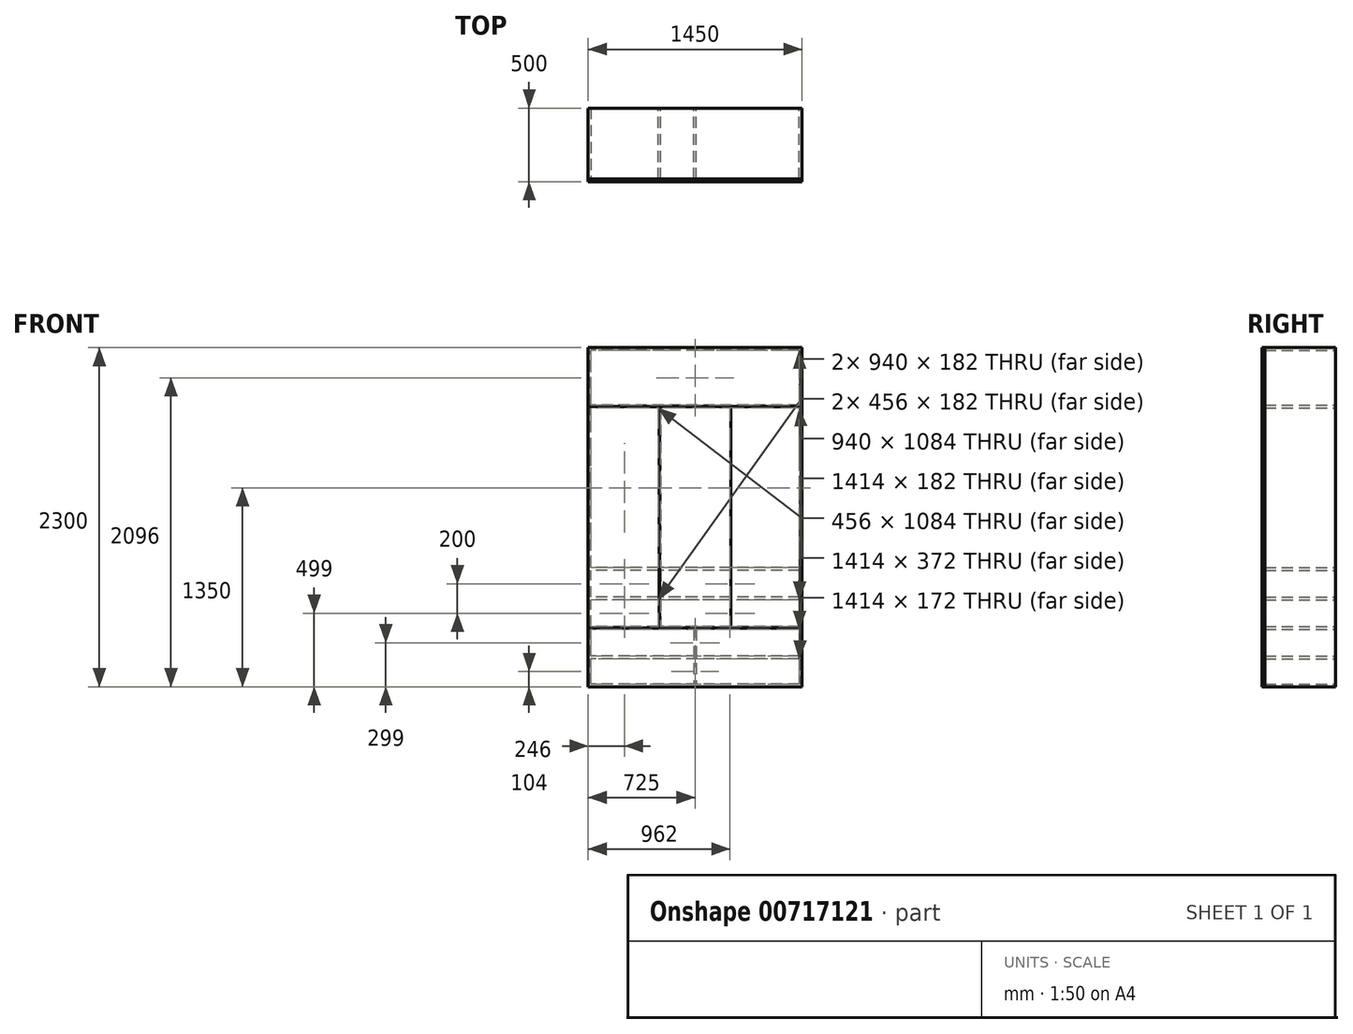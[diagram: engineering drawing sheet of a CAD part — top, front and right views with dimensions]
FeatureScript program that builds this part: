
annotation { "Feature Type Name" : "Feature", "Feature Type Description" : "" }
export const myFeature = defineFeature(function(context is Context, id is Id, definition is map)
    precondition{}
    {
        {
            var Q0;
            Q0=qCreatedBy(makeId("Front.planeOp"),FACE);
            var sketch = newSketch(context, id + "F0", { "sketchPlane" : qUnion([Q0])});
            skLineSegment(sketch, "E0.bottom", {"start": v(725, -1150) * mm, "end": v(-725, -1150) * mm});
            skLineSegment(sketch, "E0.top", {"start": v(725, 1150) * mm, "end": v(-725, 1150) * mm});
            skLineSegment(sketch, "E0.left", {"start": v(725, -1150) * mm, "end": v(725, 1150) * mm});
            skLineSegment(sketch, "E0.right", {"start": v(-725, -1150) * mm, "end": v(-725, 1150) * mm});
            skPoint(sketch, "E0.middle", {"position": v(0, 0) * mm});
            skSolve(sketch);
        }
        {
            var Q0;
            Q0 = qSketchRegion(id + "F0", true);
            extrude(context, id + "F1", {"entities" : qUnion([Q0]), "depth" : 500 * mm, "offsetDistance" : 25 * mm});
        }
        {
            var Q0;
            Q0=makeQuery(id+"F1.opExtrude","CAP_FACE",FACE,{"disambiguationData":[OSD([sQuery(id+"F0.wireOp",EDGE,"E0.bottom"),sQuery(id+"F0.wireOp",EDGE,"E0.top"),sQuery(id+"F0.wireOp",EDGE,"E0.left"),sQuery(id+"F0.wireOp",EDGE,"E0.right")])],"isStart":false});
            var sketch = newSketch(context, id + "F2", { "sketchPlane" : qUnion([Q0])});
            skLineSegment(sketch, "E1.0.left", {"start": v(-725, 752) * mm, "end": v(725, 752) * mm});
            skLineSegment(sketch, "E1.0.right", {"start": v(-725, 750) * mm, "end": v(-243, 750) * mm});
            skLineSegment(sketch, "E1.1.left", {"start": v(243, 750) * mm, "end": v(243, -750) * mm});
            skLineSegment(sketch, "E1.1.right", {"start": v(241, 750) * mm, "end": v(241, -750) * mm});
            skLineSegment(sketch, "E1.2.left", {"start": v(-725, -750) * mm, "end": v(-243, -750) * mm});
            skLineSegment(sketch, "E1.2.right", {"start": v(-725, -752) * mm, "end": v(725, -752) * mm});
            skLineSegment(sketch, "E1.3.left", {"start": v(-241, 750) * mm, "end": v(-241, -750) * mm});
            skLineSegment(sketch, "E1.3.right", {"start": v(-243, 750) * mm, "end": v(-243, -750) * mm});
            skLineSegment(sketch, "E2", {"start": v(-725, 752) * mm, "end": v(-725, 750) * mm});
            skLineSegment(sketch, "E3", {"start": v(725, 752) * mm, "end": v(725, 750) * mm});
            skLineSegment(sketch, "E4.trimOffspring", {"start": v(-241, 750) * mm, "end": v(241, 750) * mm});
            skLineSegment(sketch, "E5.trimOffspring", {"start": v(243, 750) * mm, "end": v(725, 750) * mm});
            skLineSegment(sketch, "E6.trimOffspring", {"start": v(243, -750) * mm, "end": v(725, -750) * mm});
            skLineSegment(sketch, "E7.trimOffspring", {"start": v(-241, -750) * mm, "end": v(241, -750) * mm});
            skLineSegment(sketch, "E8", {"start": v(-725, -750) * mm, "end": v(-725, -752) * mm});
            skLineSegment(sketch, "E9", {"start": v(725, -750) * mm, "end": v(725, -752) * mm});
            skSolve(sketch);
        }
        {
            var Q0;
            Q0 = qSketchRegion(id + "F2", true);
            extrude(context, id + "F3", {"entities" : qUnion([Q0]), "operationType" : NewBodyOperationType.REMOVE, "oppositeDirection" : true, "depth" : 18 * mm, "offsetDistance" : 25 * mm});
        }
        {
            var Q0;
            Q0=makeQuery(id+"F1.opExtrude","SWEPT_FACE",FACE,{"disambiguationData":[OSD([sQuery(id+"F0.wireOp",EDGE,"E0.left")])]});
            var sketch = newSketch(context, id + "F4", { "sketchPlane" : qUnion([Q0])});
            skLineSegment(sketch, "E10", {"start": v(-482, 1150) * mm, "end": v(-482, -1150) * mm});
            skLineSegment(sketch, "E11.0", {"start": v(-480, 1150) * mm, "end": v(-480, -1150) * mm});
            skLineSegment(sketch, "E12.6", {"start": v(-480, -747) * mm, "end": v(-480, -753) * mm});
            skLineSegment(sketch, "E12.9", {"start": v(-480, 753) * mm, "end": v(-480, 747) * mm});
            skLineSegment(sketch, "E13", {"start": v(-482, 1150) * mm, "end": v(-480, 1150) * mm});
            skLineSegment(sketch, "E14", {"start": v(-482, -1150) * mm, "end": v(-480, -1150) * mm});
            skSolve(sketch);
        }
        {
            var Q0;
            Q0 = qSketchRegion(id + "F4", true);
            extrude(context, id + "F5", {"entities" : qUnion([Q0]), "operationType" : NewBodyOperationType.REMOVE, "oppositeDirection" : true, "depth" : 1450 * mm, "offsetDistance" : 25 * mm});
        }
        {
            var Q0;
            Q0=makeQuery(id+"F0.imprint","IMPRINT",FACE,{"disambiguationData":[TD([[makeQuery(id+"F0.imprint","IMPRINT",EDGE,{"derivedFrom":sQuery(id+"F0.wireOp",EDGE,"E0.bottom")}),-1.0]])]});
            var sketch = newSketch(context, id + "F6", { "sketchPlane" : qUnion([Q0])});
            skLineSegment(sketch, "E15.0", {"start": v(707, 1132) * mm, "end": v(-707, 1132) * mm});
            skLineSegment(sketch, "E15.1", {"start": v(707, 1132) * mm, "end": v(707, -1132) * mm});
            skLineSegment(sketch, "E15.2", {"start": v(707, -1132) * mm, "end": v(-707, -1132) * mm});
            skLineSegment(sketch, "E15.3", {"start": v(-707, -1132) * mm, "end": v(-707, 1132) * mm});
            skSolve(sketch);
        }
        {
            var Q0;
            Q0 = qSketchRegion(id + "F6", true);
            extrude(context, id + "F7", {"entities" : qUnion([Q0]), "operationType" : NewBodyOperationType.REMOVE, "depth" : 480 * mm, "offsetDistance" : 25 * mm});
        }
        {
            var Q0;
            Q0=makeQuery(id+"F0.imprint","IMPRINT",FACE,{"disambiguationData":[TD([[makeQuery(id+"F0.imprint","IMPRINT",EDGE,{"derivedFrom":sQuery(id+"F0.wireOp",EDGE,"E0.bottom")}),-1.0]])]});
            var sketch = newSketch(context, id + "F8", { "sketchPlane" : qUnion([Q0])});
            skLineSegment(sketch, "E16.0.left", {"start": v(725, -960) * mm, "end": v(-725, -960) * mm});
            skLineSegment(sketch, "E16.0.right", {"start": v(725, -942) * mm, "end": v(-233, -942) * mm});
            skLineSegment(sketch, "E16.1.left", {"start": v(725, -760) * mm, "end": v(-233, -760) * mm});
            skLineSegment(sketch, "E16.1.right", {"start": v(725, -742) * mm, "end": v(-233, -742) * mm});
            skLineSegment(sketch, "E16.2.left", {"start": v(-233, 742) * mm, "end": v(-233, -342) * mm});
            skLineSegment(sketch, "E16.2.right", {"start": v(-251, 742) * mm, "end": v(-251, -342) * mm});
            skLineSegment(sketch, "E16.3.left", {"start": v(725, 742) * mm, "end": v(-233, 742) * mm});
            skLineSegment(sketch, "E16.3.right", {"start": v(725, 760) * mm, "end": v(-725, 760) * mm});
            skLineSegment(sketch, "E16.4.left", {"start": v(725, -360) * mm, "end": v(-233, -360) * mm});
            skLineSegment(sketch, "E16.4.right", {"start": v(725, -342) * mm, "end": v(-233, -342) * mm});
            skLineSegment(sketch, "E16.5.left", {"start": v(725, -560) * mm, "end": v(-233, -560) * mm});
            skLineSegment(sketch, "E16.5.right", {"start": v(725, -542) * mm, "end": v(-233, -542) * mm});
            skLineSegment(sketch, "E17.0", {"start": v(725, 760) * mm, "end": v(725, 742) * mm});
            skLineSegment(sketch, "E18.trimOffspring", {"start": v(-251, 742) * mm, "end": v(-725, 742) * mm});
            skLineSegment(sketch, "E19.0", {"start": v(-725, -960) * mm, "end": v(-725, -942) * mm});
            skLineSegment(sketch, "E20.trimOffspring", {"start": v(-725, 742) * mm, "end": v(-725, 760) * mm});
            skLineSegment(sketch, "E21.trimOffspring", {"start": v(-725, -360) * mm, "end": v(-725, -342) * mm});
            skLineSegment(sketch, "E22.trimOffspring", {"start": v(-251, -342) * mm, "end": v(-725, -342) * mm});
            skLineSegment(sketch, "E23.trimOffspring", {"start": v(-251, -360) * mm, "end": v(-251, -542) * mm});
            skLineSegment(sketch, "E24.trimOffspring", {"start": v(-251, -360) * mm, "end": v(-725, -360) * mm});
            skLineSegment(sketch, "E25.trimOffspring", {"start": v(-233, -360) * mm, "end": v(-233, -542) * mm});
            skLineSegment(sketch, "E26.trimOffspring", {"start": v(-251, -560) * mm, "end": v(-251, -742) * mm});
            skLineSegment(sketch, "E27.trimOffspring", {"start": v(-251, -542) * mm, "end": v(-725, -542) * mm});
            skLineSegment(sketch, "E28.trimOffspring", {"start": v(-251, -560) * mm, "end": v(-725, -560) * mm});
            skLineSegment(sketch, "E29.trimOffspring", {"start": v(-233, -560) * mm, "end": v(-233, -742) * mm});
            skLineSegment(sketch, "E30.trimOffspring", {"start": v(-251, -742) * mm, "end": v(-725, -742) * mm});
            skLineSegment(sketch, "E31.trimOffspring", {"start": v(-251, -760) * mm, "end": v(-725, -760) * mm});
            skLineSegment(sketch, "E32.trimOffspring", {"start": v(-725, -560) * mm, "end": v(-725, -542) * mm});
            skLineSegment(sketch, "E33.trimOffspring", {"start": v(-725, -760) * mm, "end": v(-725, -742) * mm});
            skLineSegment(sketch, "E34.trimOffspring", {"start": v(-251, -942) * mm, "end": v(-725, -942) * mm});
            skLineSegment(sketch, "E35.trimOffspring", {"start": v(725, -342) * mm, "end": v(725, -360) * mm});
            skLineSegment(sketch, "E36.trimOffspring", {"start": v(725, -542) * mm, "end": v(725, -560) * mm});
            skLineSegment(sketch, "E37.trimOffspring", {"start": v(725, -742) * mm, "end": v(725, -760) * mm});
            skLineSegment(sketch, "E38.trimOffspring", {"start": v(725, -942) * mm, "end": v(725, -960) * mm});
            skLineSegment(sketch, "E39", {"start": v(-233, -760) * mm, "end": v(-251, -760) * mm});
            skLineSegment(sketch, "E40", {"start": v(-233, -942) * mm, "end": v(-251, -942) * mm});
            skSolve(sketch);
        }
        {
            var Q0;
            Q0 = qSketchRegion(id + "F8", true);
            extrude(context, id + "F9", {"entities" : qUnion([Q0]), "operationType" : NewBodyOperationType.ADD, "depth" : 480 * mm, "offsetDistance" : 25 * mm});
        }
        {
            var Q0;
            Q0=makeQuery(id+"F0.imprint","IMPRINT",FACE,{"disambiguationData":[TD([[makeQuery(id+"F0.imprint","IMPRINT",EDGE,{"derivedFrom":sQuery(id+"F0.wireOp",EDGE,"E0.bottom")}),-1.0]])]});
            var sketch = newSketch(context, id + "F10", { "sketchPlane" : qUnion([Q0])});
            skLineSegment(sketch, "E41.0.left", {"start": v(9, -760) * mm, "end": v(9, -1132) * mm});
            skLineSegment(sketch, "E41.0.right", {"start": v(-9, -760) * mm, "end": v(-9, -1132) * mm});
            skLineSegment(sketch, "E42.0", {"start": v(9, -760) * mm, "end": v(-9, -760) * mm});
            skLineSegment(sketch, "E43.0", {"start": v(9, -1132) * mm, "end": v(-9, -1132) * mm});
            skPoint(sketch, "E44.orphan", {"position": v(707, -760) * mm});
            skPoint(sketch, "E45.orphan", {"position": v(-707, -760) * mm});
            skPoint(sketch, "E46.orphan", {"position": v(-707, -1132) * mm});
            skPoint(sketch, "E47.orphan", {"position": v(707, -1132) * mm});
            skSolve(sketch);
        }
        {
            var Q0;
            Q0 = qSketchRegion(id + "F10", true);
            extrude(context, id + "F11", {"entities" : qUnion([Q0]), "depth" : 480 * mm, "offsetDistance" : 25 * mm});
        }
    });
